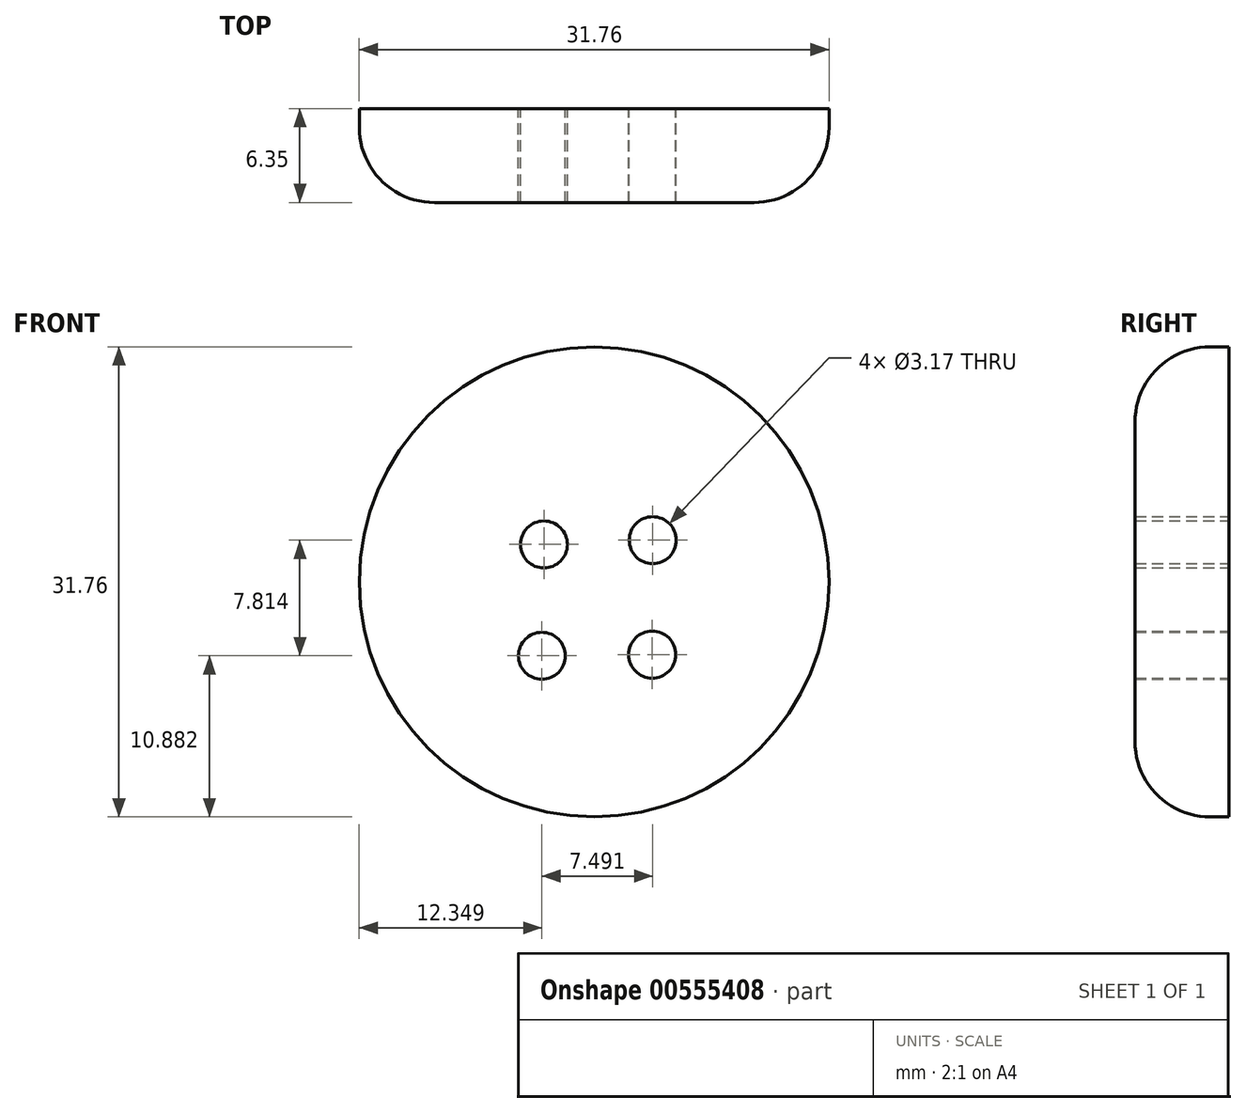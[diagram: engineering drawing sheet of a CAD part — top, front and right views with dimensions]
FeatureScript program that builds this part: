
annotation { "Feature Type Name" : "Feature", "Feature Type Description" : "" }
export const myFeature = defineFeature(function(context is Context, id is Id, definition is map)
    precondition{}
    {
        {
            var Q0;
            Q0=qCreatedBy(makeId("Front.planeOp"),FACE);
            var sketch = newSketch(context, id + "F0", { "sketchPlane" : qUnion([Q0])});
            skCircle(sketch, "E0", {"center": v(0, 0) * mm, "radius": 15.88 * mm});
            skPoint(sketch, "E1", {"position": v(-6.7, 6.1) * mm});
            skPoint(sketch, "E2", {"position": v(-7.1, -8.67) * mm});
            skPoint(sketch, "E3", {"position": v(7.49, -8.67) * mm});
            skPoint(sketch, "E4", {"position": v(7.49, 6.5) * mm});
            skSolve(sketch);
        }
        {
            var Q0;
            Q0=makeQuery(id+"F0.imprint","IMPRINT",FACE,{"disambiguationData":[TD([[makeQuery(id+"F0.imprint","IMPRINT",EDGE,{"derivedFrom":sQuery(id+"F0.wireOp",EDGE,"E0")}),1.0]])]});
            var sketch = newSketch(context, id + "F1", { "sketchPlane" : qUnion([Q0])});
            skCircle(sketch, "E5", {"center": v(-3.4, 2.53) * mm, "radius": 3.18 * mm});
            skCircle(sketch, "E6", {"center": v(3.96, 2.82) * mm, "radius": 2.93 * mm});
            skCircle(sketch, "E7", {"center": v(3.93, -4.91) * mm, "radius": 2.92 * mm});
            skCircle(sketch, "E8", {"center": v(-3.53, -5) * mm, "radius": 3.07 * mm});
            skSolve(sketch);
        }
        {
            var Q0;
            Q0=makeQuery(id+"F0.imprint","IMPRINT",FACE,{"disambiguationData":[TD([[makeQuery(id+"F0.imprint","IMPRINT",EDGE,{"derivedFrom":sQuery(id+"F0.wireOp",EDGE,"E0")}),1.0]])]});
            extrude(context, id + "F2", {"entities" : qUnion([Q0]), "depth" : 6.35 * mm, "offsetDistance" : 25.4 * mm});
        }
        {
            var Q0;
            Q0=sQuery(id+"F1.wireOp",VERTEX,"E6.center");
            var Q1;
            Q1=sQuery(id+"F1.wireOp",VERTEX,"E5.center");
            var Q2;
            Q2=sQuery(id+"F1.wireOp",VERTEX,"E8.center");
            var Q3;
            Q3=sQuery(id+"F1.wireOp",VERTEX,"E7.center");
            var Q4;
            Q4=makeQuery(id+"F2.opExtrude","SWEPT_BODY",BODY,{"disambiguationData":[OSD([sQuery(id+"F0.wireOp",EDGE,"E0")])]});
            hole(context, id + "F3", {"style" : HoleStyle.SIMPLE, "endStyle" : HoleEndStyle.THROUGH, "oppositeDirection" : true, "holeDiameter" : 3.17 * mm, "isTappedThrough" : true, "tappedDepth" : 12.7 * mm, "tapClearance" : 3, "locations" : qUnion([Q0, Q1, Q2, Q3]), "scope" : qUnion([Q4])});
        }
        {
            var Q0;
            Q0=makeQuery(id+"F2.opExtrude","CAP_EDGE",EDGE,{"disambiguationData":[OSD([sQuery(id+"F0.wireOp",EDGE,"E0")])],"isStart":false});
            fillet(context, id + "F4", {"entities" : qUnion([Q0]), "radius" : 5.08 * mm, "tangentPropagation" : true, "allowEdgeOverflow" : false});
        }
    });
